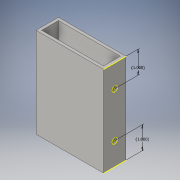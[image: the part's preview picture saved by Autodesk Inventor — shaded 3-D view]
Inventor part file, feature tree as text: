
AUTODESK INVENTOR PART (.ipt)
format: ipt  version: 2016 (Build 200138000, 138)  size: 111,104 bytes
history: native  units: in
note: dims shown in document units (in); Inventor stores cm internally (conversion verified against a paired STEP export)
features: sketch x3, extrude x2
ambient origin geometry x8: Origin, YZ Plane, XZ Plane, XY Plane, X Axis, Y Axis, Z Axis, Center Point
bodies: Solid1 (feature_tree)
feature tree (5):
  extrude  "Extrusion1"  Depth=1.0in
  extrude  "Extrusion2"  Depth=4.0in TaperAngle=0.0deg
  sketch  "Sketch4"  dims[d5=0.25in d6=1.0in d7=1.0in d8=0.125in d9=0.0in d17=1.0in d18=1.0in]
  sketch  "Sketch1"  dims[d0=3.0in d1=1.0in]
  sketch  "Sketch2"  dims[d2=0.125in d3=4.0in d4=0.0in]
